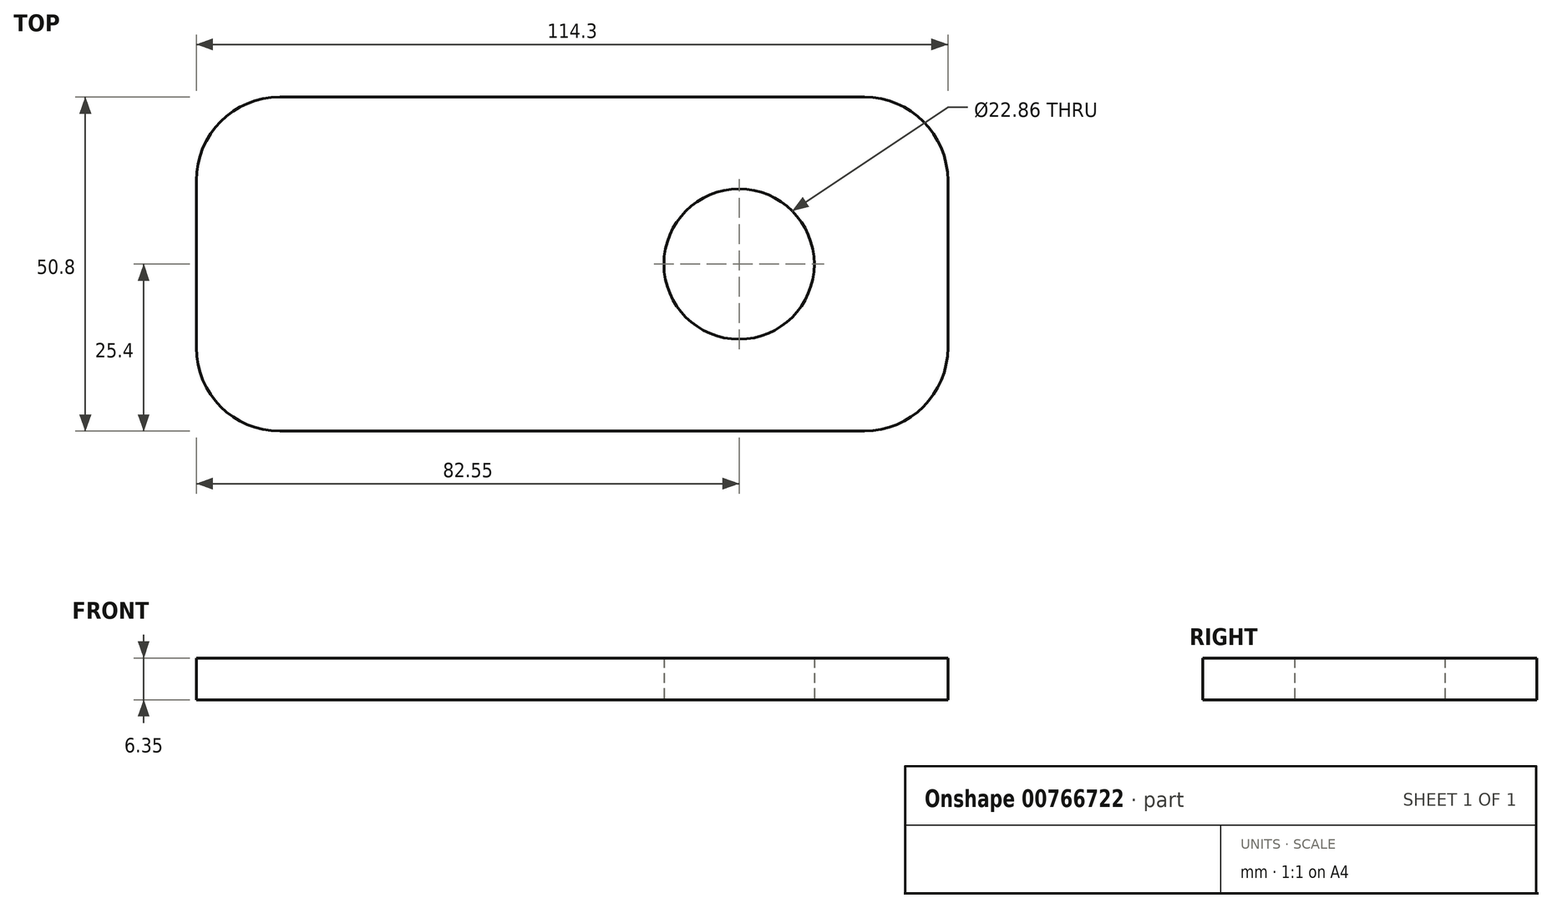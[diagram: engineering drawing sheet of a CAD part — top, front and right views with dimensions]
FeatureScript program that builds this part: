
annotation { "Feature Type Name" : "Feature", "Feature Type Description" : "" }
export const myFeature = defineFeature(function(context is Context, id is Id, definition is map)
    precondition{}
    {
        {
            var Q0;
            Q0=qCreatedBy(makeId("Top.planeOp"),FACE);
            var sketch = newSketch(context, id + "F0", { "sketchPlane" : qUnion([Q0])});
            skLineSegment(sketch, "E0.bottom", {"start": v(12.7, 0) * mm, "end": v(101.6, 0) * mm});
            skLineSegment(sketch, "E0.top", {"start": v(12.7, -50.8) * mm, "end": v(101.6, -50.8) * mm});
            skLineSegment(sketch, "E0.left", {"start": v(0, -12.7) * mm, "end": v(0, -38.1) * mm});
            skLineSegment(sketch, "E0.right", {"start": v(114.3, -12.7) * mm, "end": v(114.3, -38.1) * mm});
            skPoint(sketch, "E1.visualSharp", {"position": v(0, 0) * mm});
            skArc(sketch, "E1.filletArc", {"start": v(12.7, 0) * mm, "mid": v(3.72, -3.72) * mm, "end": v(0, -12.7) * mm});
            skPoint(sketch, "E2.visualSharp", {"position": v(114.3, 0) * mm});
            skArc(sketch, "E2.filletArc", {"start": v(114.3, -12.7) * mm, "mid": v(110.58, -3.72) * mm, "end": v(101.6, 0) * mm});
            skPoint(sketch, "E3.visualSharp", {"position": v(114.3, -50.8) * mm});
            skArc(sketch, "E3.filletArc", {"start": v(101.6, -50.8) * mm, "mid": v(110.58, -47.08) * mm, "end": v(114.3, -38.1) * mm});
            skPoint(sketch, "E4.visualSharp", {"position": v(0, -50.8) * mm});
            skArc(sketch, "E4.filletArc", {"start": v(0, -38.1) * mm, "mid": v(3.72, -47.08) * mm, "end": v(12.7, -50.8) * mm});
            skLineSegment(sketch, "E5", {"start": v(50.8, 0) * mm, "end": v(50.8, -50.8) * mm});
            skCircle(sketch, "E6", {"center": v(82.55, -25.4) * mm, "radius": 11.43 * mm});
            skSolve(sketch);
        }
        {
            var Q0;
            Q0=makeQuery(id+"F0.imprint","IMPRINT",FACE,{"disambiguationData":[TD([[makeQuery(id+"F0.imprint","IMPRINT",EDGE,{"derivedFrom":sQuery(id+"F0.wireOp",EDGE,"E0.left")}),1.0]])]});
            var Q1;
            Q1=makeQuery(id+"F0.imprint","IMPRINT",FACE,{"disambiguationData":[TD([[makeQuery(id+"F0.imprint","IMPRINT",EDGE,{"derivedFrom":sQuery(id+"F0.wireOp",EDGE,"E0.right")}),-1.0]])]});
            extrude(context, id + "F1", {"entities" : qUnion([Q0, Q1]), "depth" : 6.35 * mm, "offsetDistance" : 25.4 * mm});
        }
    });
